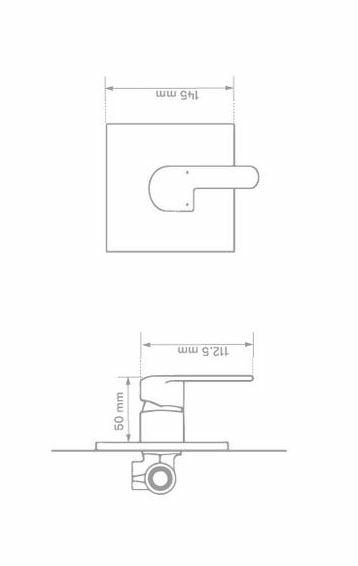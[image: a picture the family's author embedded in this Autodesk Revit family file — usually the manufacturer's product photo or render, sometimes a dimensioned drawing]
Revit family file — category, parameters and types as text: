
# Revit family: 01-1503-11 MEZCLADOR LAVAMANOS 8” PIANA
name_source: partatom
category: Plumbing Fixtures
revit_build: Autodesk Revit 2018 (Build: 20170223_1515(x64)
units: mm (PartAtom-declared; Revit-internal decimal feet)

## family parameters
Cut with Voids When Loaded = No
Host = Face
OmniClass Number = 23.31.11.00
Part Type = Normal
Room Calculation Point = No
Round Connector Dimension = Use Diameter
Shared = No

## types (1)
- 01-1503-11
    Alto - Aireador = 68.5 mm  [stored 0.224738 ft]
    Ancho manija = 75 mm
    CW Connection = Yes
    Default Elevation = 0 mm  [stored 0 ft]
    Description = Bimando baño
    Eje ( Rosca) = 203.2 mm  [stored 0.666667 ft]
    Eje-Aireador = 122.6 mm  [stored 0.402231 ft]
    HW Connection = Yes
    Link ficha tecnica = http://infotecnica.gricol.com
    Manufacturer = Gricol
    Model = 01-1503-11
    Plastico ABS Cromado = Plastico - ABS Cromado
    Product Name = MEZCLADOR LAVAMANOS 8” PIANA
    Type Image = MEZCLADOR LAVAMANOS 8” PIANA.jpg
    URL = https://www.gricol.com
    Vent Connection = No
    Waste Connection = No

note: [stored X ft] marks values corroborated as IEEE doubles in the binary element streams (Revit-internal decimal feet)

## geometry (parser evidence)
native form markers: Blend x4, Sweep x8
no freeform markers — native parametric forms only
